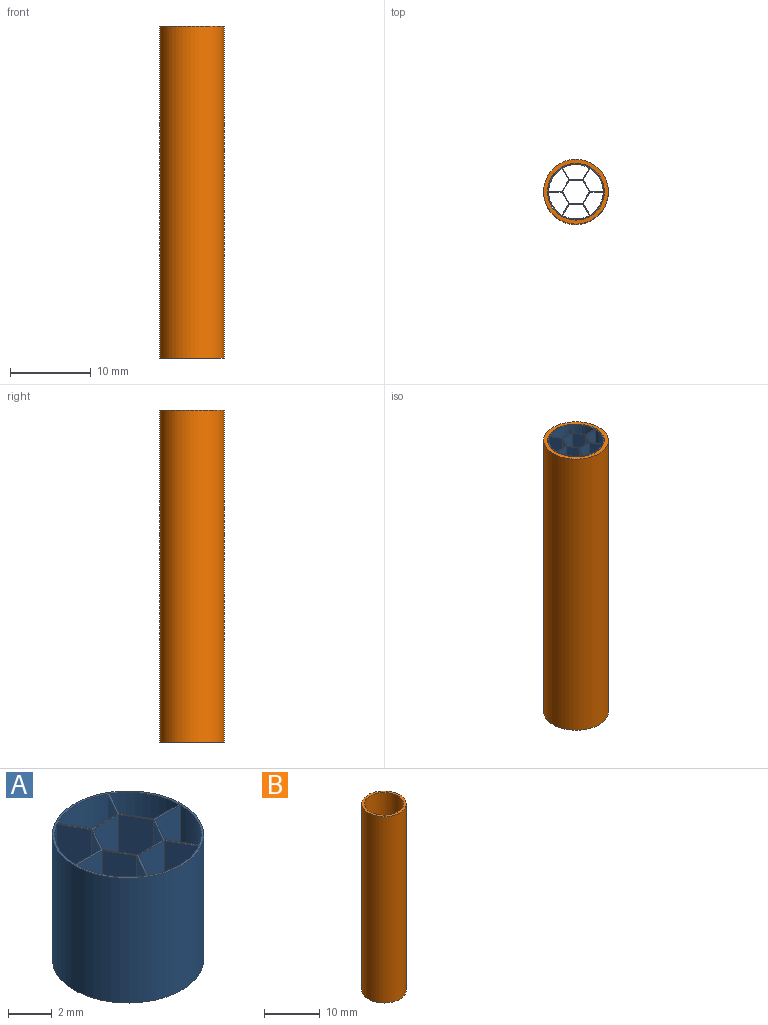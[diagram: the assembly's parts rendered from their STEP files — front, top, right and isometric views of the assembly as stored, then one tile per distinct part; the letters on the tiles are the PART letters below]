
ASSEMBLY  parts=2 mates=1
PART A: 33 faces, bbox 7x7x7 mm
  f0: plane 6.95x6.95mm, normal (0,0,1), area 4.1mm2, adj f2,f3,f4,f5,f6,f7,f8,f9
  f1: plane 6.95x6.95mm, normal (0,0,-1), area 4.1mm2, adj f2,f3,f4,f5,f6,f7,f8,f9
  f2: cylinder r=3.47mm len=7mm, axis (0,0,-1), area 152.8mm2, adj f0,f1
  f3: plane 7x1.44mm, normal (-0.87,0.5,0), area 11.6mm2, adj f0,f1,f4,f8
  f4: plane 7x1.66mm, normal (0,1,0), area 11.6mm2, adj f0,f1,f3,f5
  f5: plane 7x1.44mm, normal (0.87,0.5,0), area 11.6mm2, adj f0,f1,f4,f6
  f6: plane 7x1.44mm, normal (0.87,-0.5,0), area 11.6mm2, adj f0,f1,f5,f7
  f7: plane 7x1.66mm, normal (0,-1,0), area 11.6mm2, adj f0,f1,f6,f8
  f8: plane 7x1.44mm, normal (-0.87,-0.5,0), area 11.6mm2, adj f0,f1,f3,f7
  f9: plane 7x1.64mm, normal (0,1,0), area 11.5mm2, adj f0,f1,f10,f12
  f10: cylinder r=3.36mm len=7mm, axis (0,0,-1), area 24mm2, adj f0,f1,f9,f11
  f11: plane 7x1.42mm, normal (-0.87,-0.5,0), area 11.5mm2, adj f0,f1,f10,f12
  f12: plane 7x1.42mm, normal (-0.87,0.5,0), area 11.5mm2, adj f0,f1,f9,f11
  f13: plane 7x1.42mm, normal (0.87,0.5,0), area 11.5mm2, adj f0,f1,f14,f16
  f14: cylinder r=3.36mm len=7mm, axis (0,0,-1), area 24mm2, adj f0,f1,f13,f15
  f15: plane 7x1.42mm, normal (-0.87,0.5,0), area 11.5mm2, adj f0,f1,f14,f16
  f16: plane 7x1.64mm, normal (0,1,0), area 11.5mm2, adj f0,f1,f13,f15
  f17: plane 7x1.42mm, normal (0.87,-0.5,0), area 11.5mm2, adj f0,f1,f18,f20
  f18: cylinder r=3.36mm len=7mm, axis (0,0,-1), area 24mm2, adj f0,f1,f17,f19
  f19: plane 7x1.64mm, normal (0,1,0), area 11.5mm2, adj f0,f1,f18,f20
  f20: plane 7x1.42mm, normal (0.87,0.5,0), area 11.5mm2, adj f0,f1,f17,f19
  f21: plane 7x1.64mm, normal (0,-1,0), area 11.5mm2, adj f0,f1,f22,f24
  f22: cylinder r=3.36mm len=7mm, axis (0,0,-1), area 24mm2, adj f0,f1,f21,f23
  f23: plane 7x1.42mm, normal (0.87,0.5,0), area 11.5mm2, adj f0,f1,f22,f24
  f24: plane 7x1.42mm, normal (0.87,-0.5,0), area 11.5mm2, adj f0,f1,f21,f23
  f25: plane 7x1.42mm, normal (-0.87,0.5,0), area 11.5mm2, adj f0,f1,f26,f28
  f26: cylinder r=3.36mm len=7mm, axis (0,0,-1), area 24mm2, adj f0,f1,f25,f27
  f27: plane 7x1.64mm, normal (0,-1,0), area 11.5mm2, adj f0,f1,f26,f28
  f28: plane 7x1.42mm, normal (-0.87,-0.5,0), area 11.5mm2, adj f0,f1,f25,f27
  f29: plane 7x1.42mm, normal (-0.87,-0.5,0), area 11.5mm2, adj f0,f1,f30,f32
  f30: cylinder r=3.36mm len=7mm, axis (0,0,-1), area 24mm2, adj f0,f1,f29,f31
  f31: plane 7x1.42mm, normal (0.87,-0.5,0), area 11.5mm2, adj f0,f1,f30,f32
  f32: plane 7x1.64mm, normal (0,-1,0), area 11.5mm2, adj f0,f1,f29,f31
PART B: 4 faces, bbox 8x8x41 mm
  f0: cylinder r=4mm len=41mm, axis (0,0,-1), area 1030.4mm2, adj f1,f2
  f1: plane 8x8mm, normal (0,0,1), area 11.8mm2, adj f0,f3
  f2: plane 8x8mm, normal (0,0,-1), area 11.8mm2, adj f0,f3
  f3: cylinder r=3.5mm len=41mm, axis (0,0,1), area 901.6mm2, adj f1,f2
PLACE A t=(-2.83,-4.09,9.81)mm
PLACE B t=(-2.83,-4.09,-24.19)mm
MATE fastened A.f2 <-> B.f0  axis (0,0,-1) through (-2.83,-4.09,13.31)mm
